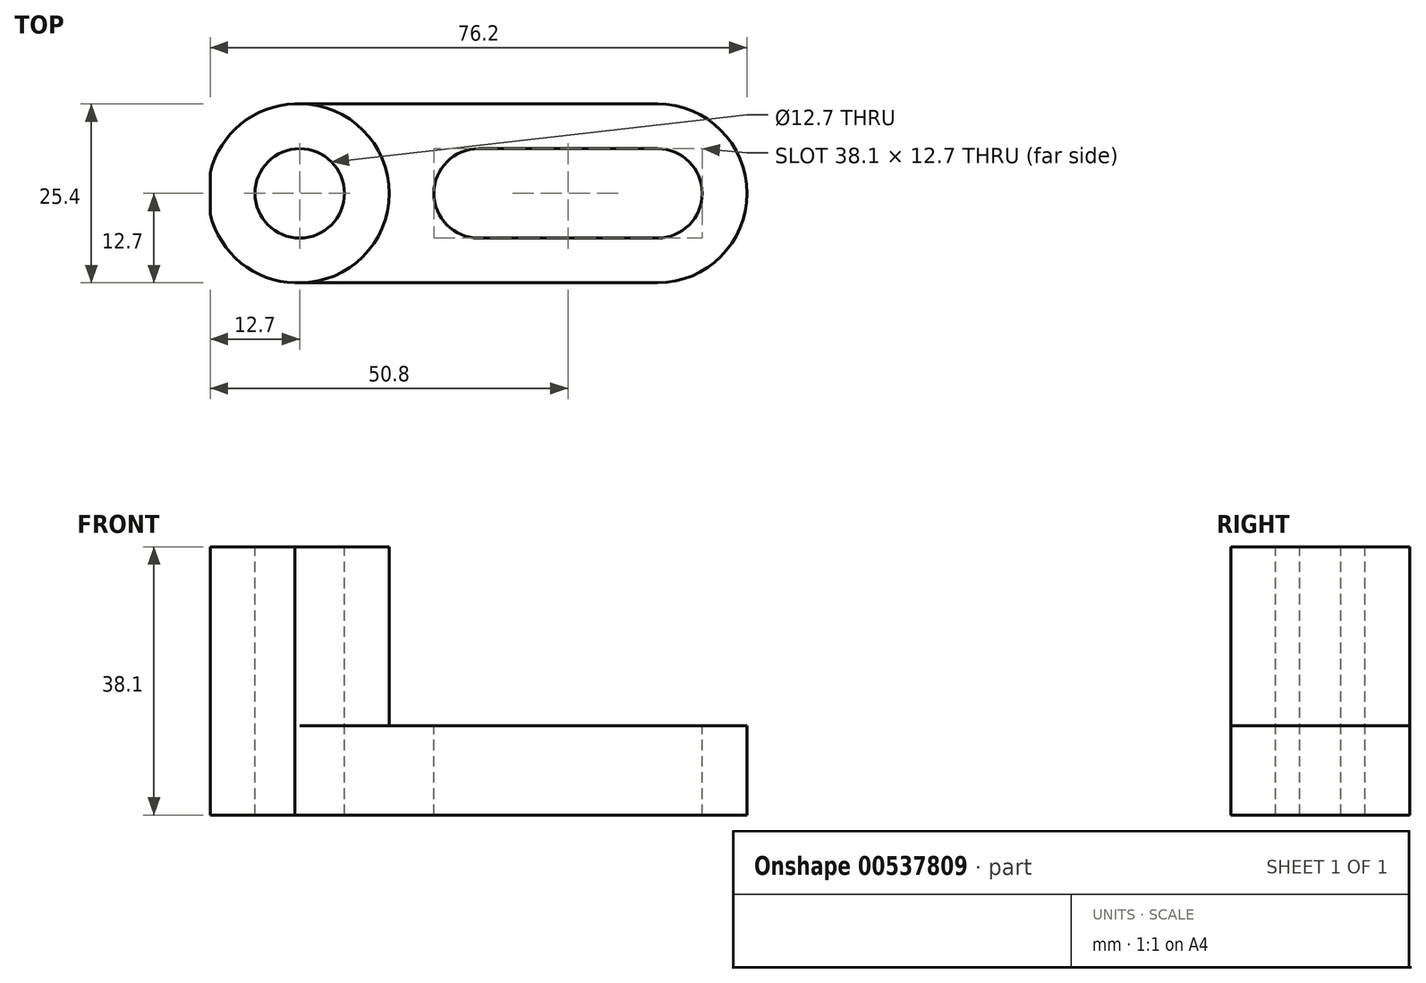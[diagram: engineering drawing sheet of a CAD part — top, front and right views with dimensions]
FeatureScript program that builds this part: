
annotation { "Feature Type Name" : "Feature", "Feature Type Description" : "" }
export const myFeature = defineFeature(function(context is Context, id is Id, definition is map)
    precondition{}
    {
        {
            var Q0;
            Q0=qCreatedBy(makeId("Front.planeOp"),FACE);
            var sketch = newSketch(context, id + "F0", { "sketchPlane" : qUnion([Q0])});
            skLineSegment(sketch, "E0", {"start": v(0, 0) * mm, "end": v(0, 38.1) * mm});
            skLineSegment(sketch, "E1", {"start": v(0, 38.1) * mm, "end": v(25.4, 38.1) * mm});
            skLineSegment(sketch, "E2", {"start": v(25.4, 38.1) * mm, "end": v(25.4, 12.7) * mm});
            skLineSegment(sketch, "E3", {"start": v(25.4, 12.7) * mm, "end": v(76.2, 12.7) * mm});
            skLineSegment(sketch, "E4", {"start": v(76.2, 12.7) * mm, "end": v(76.2, 0) * mm});
            skLineSegment(sketch, "E5", {"start": v(76.2, 0) * mm, "end": v(0, 0) * mm});
            skSolve(sketch);
        }
        {
            var Q0;
            Q0=makeQuery(id+"F0.imprint","IMPRINT",FACE,{"disambiguationData":[TD([[makeQuery(id+"F0.imprint","IMPRINT",EDGE,{"derivedFrom":sQuery(id+"F0.wireOp",EDGE,"E0")}),-1.0]])]});
            extrude(context, id + "F1", {"entities" : qUnion([Q0]), "depth" : 25.4 * mm, "offsetDistance" : 25.4 * mm});
        }
        {
            var Q0;
            Q0=makeQuery(id+"F1.opExtrude","SWEPT_FACE",FACE,{"disambiguationData":[OSD([sQuery(id+"F0.wireOp",EDGE,"E1")])]});
            var sketch = newSketch(context, id + "F2", { "sketchPlane" : qUnion([Q0])});
            skCircle(sketch, "E6", {"center": v(12.7, -12.7) * mm, "radius": 6.35 * mm});
            skPoint(sketch, "E6.centerSnap0", {"position": v(12.7, -25.4) * mm});
            skArc(sketch, "E7", {"start": v(12.7, 0) * mm, "mid": v(-0.35, -12.7) * mm, "end": v(12.7, -25.4) * mm});
            skArc(sketch, "E8", {"start": v(12.7, -25.4) * mm, "mid": v(25.55, -12.7) * mm, "end": v(12.7, 0) * mm});
            skSolve(sketch);
        }
        {
            var Q0;
            {var subQ0=sQuery(id+"F2.wireOp",EDGE,"E7");var subQ1=sQuery(id+"F0.wireOp",EDGE,"E1");var subQ4=makeQuery(id+"F1.opExtrude","CAP_EDGE",EDGE,{"disambiguationData":[OSD([subQ1])],"isStart":false});var subQ5=makeQuery(id+"F2.imprint","INTERSECT",VERTEX,{"derivedFrom":[subQ4,subQ0]});Q0=makeQuery(id+"F2.imprint","IMPRINT",FACE,{"disambiguationData":[TD([[makeQuery(id+"F2.imprint","IMPRINT",EDGE,{"disambiguationData":[TD([[subQ5,1.0]])],"derivedFrom":subQ0}),-1.0]])]});}
            var Q1;
            {var subQ0=sQuery(id+"F2.wireOp",EDGE,"E7");var subQ1=sQuery(id+"F0.wireOp",EDGE,"E1");var subQ2=makeQuery(id+"F1.opExtrude","CAP_EDGE",EDGE,{"disambiguationData":[OSD([subQ1])],"isStart":true});var subQ3=makeQuery(id+"F2.imprint","INTERSECT",VERTEX,{"derivedFrom":[subQ2,subQ0]});Q1=makeQuery(id+"F2.imprint","IMPRINT",FACE,{"disambiguationData":[TD([[makeQuery(id+"F2.imprint","IMPRINT",EDGE,{"disambiguationData":[TD([[subQ3,-1.0]])],"derivedFrom":subQ0}),-1.0]])]});}
            var Q2;
            Q2=makeQuery(id+"F2.imprint","IMPRINT",FACE,{"disambiguationData":[TD([[makeQuery(id+"F2.imprint","IMPRINT",EDGE,{"derivedFrom":sQuery(id+"F2.wireOp",EDGE,"E6")}),1.0]])]});
            extrude(context, id + "F3", {"entities" : qUnion([Q0, Q1, Q2]), "operationType" : NewBodyOperationType.REMOVE, "oppositeDirection" : true, "depth" : 38.1 * mm, "offsetDistance" : 25.4 * mm});
        }
        {
            var Q0;
            Q0=makeQuery(id+"F1.opExtrude","SWEPT_FACE",FACE,{"disambiguationData":[OSD([sQuery(id+"F0.wireOp",EDGE,"E1")])]});
            var sketch = newSketch(context, id + "F4", { "sketchPlane" : qUnion([Q0])});
            skArc(sketch, "E9", {"start": v(12.7, -25.4) * mm, "mid": v(25.4, -12.7) * mm, "end": v(12.7, 0) * mm});
            skSolve(sketch);
        }
        {
            var Q0;
            {var subQ0=sQuery(id+"F4.wireOp",EDGE,"E9");var subQ1=sQuery(id+"F0.wireOp",EDGE,"E1");var subQ2=makeQuery(id+"F1.opExtrude","CAP_EDGE",EDGE,{"disambiguationData":[OSD([subQ1])],"isStart":true});var subQ3=makeQuery(id+"F4.imprint","INTERSECT",VERTEX,{"derivedFrom":[subQ2,subQ0]});Q0=makeQuery(id+"F4.imprint","IMPRINT",FACE,{"disambiguationData":[TD([[makeQuery(id+"F4.imprint","IMPRINT",EDGE,{"disambiguationData":[TD([[subQ3,1.0]])],"derivedFrom":subQ0}),-1.0]])]});}
            var Q1;
            {var subQ0=sQuery(id+"F4.wireOp",EDGE,"E9");var subQ1=sQuery(id+"F0.wireOp",EDGE,"E1");var subQ2=makeQuery(id+"F1.opExtrude","CAP_EDGE",EDGE,{"disambiguationData":[OSD([subQ1])],"isStart":false});var subQ3=makeQuery(id+"F4.imprint","INTERSECT",VERTEX,{"derivedFrom":[subQ2,subQ0]});Q1=makeQuery(id+"F4.imprint","IMPRINT",FACE,{"disambiguationData":[TD([[makeQuery(id+"F4.imprint","IMPRINT",EDGE,{"disambiguationData":[TD([[subQ3,-1.0]])],"derivedFrom":subQ0}),-1.0]])]});}
            extrude(context, id + "F5", {"entities" : qUnion([Q0, Q1]), "operationType" : NewBodyOperationType.REMOVE, "oppositeDirection" : true, "depth" : 25.4 * mm, "offsetDistance" : 25.4 * mm});
        }
        {
            var Q0;
            {var subQ0=sQuery(id+"F0.wireOp",EDGE,"E1");var subQ1=makeQuery(id+"F1.opExtrude","CAP_EDGE",EDGE,{"disambiguationData":[OSD([subQ0])],"isStart":true});var subQ2=sQuery(id+"F0.wireOp",EDGE,"E2");var subQ3=makeQuery(id+"F1.opExtrude","SWEPT_EDGE",EDGE,{"disambiguationData":[OSD([subQ0,subQ2])]});var subQ4=makeQuery(id+"F4.imprint","INTERSECT",VERTEX,{"derivedFrom":[subQ3,subQ1]});var subQ5=sQuery(id+"F4.wireOp",EDGE,"E9");var subQ6=makeQuery(id+"F4.imprint","INTERSECT",VERTEX,{"derivedFrom":[subQ1,subQ5]});var subQ8=makeQuery(id+"F1.opExtrude","CAP_EDGE",EDGE,{"disambiguationData":[OSD([subQ0])],"isStart":false});var subQ9=makeQuery(id+"F4.imprint","INTERSECT",VERTEX,{"derivedFrom":[subQ3,subQ8]});var subQ10=makeQuery(id+"F4.imprint","INTERSECT",VERTEX,{"derivedFrom":[subQ8,subQ5]});Q0=makeQuery(id+"F5.boolean.opBoolean","MERGE",FACE,{"derivedFrom":[makeQuery(id+"F1.opExtrude","SWEPT_FACE",FACE,{"disambiguationData":[OSD([sQuery(id+"F0.wireOp",EDGE,"E3")])]})],"fromTools":[makeQuery(id+"F5.opExtrude","CAP_FACE",FACE,{"disambiguationData":[OSD([subQ0,subQ2,subQ5]),TDD([makeQuery(id+"F4.imprint","IMPRINT",EDGE,{"disambiguationData":[TD([[subQ10,-1.0]])],"derivedFrom":subQ5}),makeQuery(id+"F4.imprint","IMPRINT",EDGE,{"disambiguationData":[TD([[subQ9,-1.0]])],"derivedFrom":subQ3}),makeQuery(id+"F4.imprint","IMPRINT",EDGE,{"disambiguationData":[TD([[subQ10,-1.0]])],"derivedFrom":subQ8})])],"isStart":false}),makeQuery(id+"F5.opExtrude","CAP_FACE",FACE,{"disambiguationData":[OSD([subQ0,subQ2,subQ5]),TDD([makeQuery(id+"F4.imprint","IMPRINT",EDGE,{"disambiguationData":[TD([[subQ6,1.0]])],"derivedFrom":subQ5}),makeQuery(id+"F4.imprint","IMPRINT",EDGE,{"disambiguationData":[TD([[subQ4,1.0]])],"derivedFrom":subQ3}),makeQuery(id+"F4.imprint","IMPRINT",EDGE,{"disambiguationData":[TD([[subQ6,-1.0]])],"derivedFrom":subQ1})])],"isStart":false})]});}
            var sketch = newSketch(context, id + "F6", { "sketchPlane" : qUnion([Q0])});
            skArc(sketch, "E10", {"start": v(38.1, -6.35) * mm, "mid": v(31.75, -12.7) * mm, "end": v(38.1, -19.05) * mm});
            skArc(sketch, "E11", {"start": v(63.5, -19.05) * mm, "mid": v(69.85, -12.7) * mm, "end": v(63.5, -6.35) * mm});
            skLineSegment(sketch, "E12", {"start": v(38.1, -6.35) * mm, "end": v(63.5, -6.35) * mm});
            skLineSegment(sketch, "E13", {"start": v(63.5, -6.35) * mm, "end": v(63.5, -19.05) * mm});
            skLineSegment(sketch, "E14", {"start": v(63.5, -19.05) * mm, "end": v(38.1, -19.05) * mm});
            skArc(sketch, "E15", {"start": v(63.5, -25.4) * mm, "mid": v(76.2, -12.7) * mm, "end": v(63.5, 0) * mm});
            skSolve(sketch);
        }
        {
            var Q0;
            Q0=makeQuery(id+"F6.imprint","IMPRINT",FACE,{"disambiguationData":[TD([[makeQuery(id+"F6.imprint","IMPRINT",EDGE,{"derivedFrom":sQuery(id+"F6.wireOp",EDGE,"E10")}),1.0]])]});
            var Q1;
            Q1=makeQuery(id+"F6.imprint","IMPRINT",FACE,{"disambiguationData":[TD([[makeQuery(id+"F6.imprint","IMPRINT",EDGE,{"derivedFrom":sQuery(id+"F6.wireOp",EDGE,"E11")}),1.0]])]});
            var Q2;
            {var subQ0=sQuery(id+"F6.wireOp",EDGE,"E15");var subQ3=sQuery(id+"F0.wireOp",EDGE,"E3");var subQ6=makeQuery(id+"F1.opExtrude","SWEPT_EDGE",EDGE,{"disambiguationData":[OSD([subQ3,sQuery(id+"F0.wireOp",EDGE,"E4")])]});var subQ7=makeQuery(id+"F6.imprint","INTERSECT",VERTEX,{"derivedFrom":[subQ6,subQ0]});Q2=makeQuery(id+"F6.imprint","IMPRINT",FACE,{"disambiguationData":[TD([[makeQuery(id+"F6.imprint","IMPRINT",EDGE,{"disambiguationData":[TD([[subQ7,-1.0]])],"derivedFrom":subQ0}),-1.0]])]});}
            var Q3;
            {var subQ0=sQuery(id+"F6.wireOp",EDGE,"E15");var subQ3=sQuery(id+"F0.wireOp",EDGE,"E3");var subQ6=makeQuery(id+"F1.opExtrude","SWEPT_EDGE",EDGE,{"disambiguationData":[OSD([subQ3,sQuery(id+"F0.wireOp",EDGE,"E4")])]});var subQ7=makeQuery(id+"F6.imprint","INTERSECT",VERTEX,{"derivedFrom":[subQ6,subQ0]});Q3=makeQuery(id+"F6.imprint","IMPRINT",FACE,{"disambiguationData":[TD([[makeQuery(id+"F6.imprint","IMPRINT",EDGE,{"disambiguationData":[TD([[subQ7,1.0]])],"derivedFrom":subQ0}),-1.0]])]});}
            extrude(context, id + "F7", {"entities" : qUnion([Q0, Q1, Q2, Q3]), "operationType" : NewBodyOperationType.REMOVE, "oppositeDirection" : true, "depth" : 25.4 * mm, "offsetDistance" : 25.4 * mm});
        }
    });
